# Revit family: IS_21Ventuno_T0155_BIM_IT
name_source: partatom
category: Plumbing Fixtures
revit_build: Autodesk Revit 2017 (Build: 20160225_1515(x64)
units: mm (PartAtom-declared; Revit-internal decimal feet)

## family parameters
Always vertical = No
Cut with Voids When Loaded = No
OmniClass Number = 23.45.05.14.14
OmniClass Title = Sinks/Lavatories
Part Type = Normal
Room Calculation Point = No
Round Connector Dimension = Use Diameter
Shared = No
Work Plane-Based = No

## types (1)
- T015501 - 21/VENTUNO LAVABO 75X52 BEU
    Accessori = www.idealstandard.it
    AltezzaNominale = 198 mm
    Autore = Ideal Standard
    BIMobject category = Basins
    BIMobject category code = sanitary-basins
    BIMobject main category = Sanitary
    BIMobject main category code = sanitary
    BOSUseNativeGeometries = 1
    Brand = Ideal Standard
    Brand url = http://www.idealstandard.it
    Caratteristiche = 21-Lavabo 750 mm
    CodiceABarre = 8014140342472
    CodiceDiPrestazione = EN
    Colore = Bianco
    Connessione = piombatura
    CostoDiSostituzione = 0 $
    Date of publishing = 2019_01_04
    Description = 21-Lavabo 750 mm
    DescrizioneClassifcazioneUni2015 = Wall-hung wash basins
    Desrizione = 21-Lavabo 750 mm
    Dimensione = 1850 x 820 x 820 mm
    DimensioneScarico = 0
    EAN code = https://8014140342472
    Edition number = 1
    Finitura = Bianca
    Forma = scolpito
    Garanzia = Garanzia Ideal Standard
    Grado = n/s
    IFC Classification = IfcSanitaryTerminal
    IfcEsportaCome = SanitaryTerminal
    InformazioniDiProdotto = http://www.idealstandard.it
    Installation instructions = http://www.idealstandard.it
    Installazione = http://www.idealstandard.it
    InstruzioniInstallazione = http://www.idealstandard.it
    LarghezzaNominale = 751 mm
    LunghezzaNominale = 515 mm
    Maniglia = No
    Manufacturer name = Ideal Standard
    Material main = Ceramics
    Materiale = Ceramics
    Model = T015501
    ModelloDiRiferimento = 21-Lavabo 750 mm
    NBS Reference Code = 45-35-70/369
    NBS Reference Description = Wall-Hung Wash Basins
    Nome = WashBasinSystems_21Ventuno_T015501_IdealStandard
    NomeOggettoBim = ISI_IdealStandard_WashBasinSystems_21Ventuno_T015501
    Nominal depth = 0
    Nominal height = 0
    NominalHeight = 198 mm
    NominalLength = 515 mm
    NominalWidth = 751 mm
    NumeroDiModello = T015401
    OmniClass Code = 23-31 13 00
    OmniClass Description = Sinks
    PartiDiRicambio = http://www.idealstandard.it
    PesoNetto = 20.5
    PiattoDoccia = No
    Product Guid = ec9c83e5-59f1-4d8d-9583-9215dccaf0eb
    Product SKU = T0155
    Product certification = http://www.idealstandard.it
    Product data url = https://bimobject.com
    Product family = Sanitary
    Product group = WC pans
    Product name = 21/VENTUNO WASHBASIN 75X52 WHITE
    Product url = http://www.idealstandard.it
    ProfonditaNominale = 0 mm  [stored 0 ft]
    QR code = http://bimobject.com
    Revisione = 1
    RiferimentoClassificazioneUni2015 = Pr_40_20_93_89
    SeatMaterial = 0 mm  [stored 0 ft]
    Size = 1850 x 820 x 820 mm
    SpessoreDelMateriale = 0
    SpilloverLivello = 0
    Technical description = http://www.idealstandard.it
    Telefono = 800 652 290
    TipoDiDato = Fisso
    TipoEspotazioneIfc = IfcSanitaryTerminalType
    URL = http://www.idealstandard.it
    Uniclass 2.0 Code = PR-35-93-95
    Uniclass 2.0 Description = Wc Seats And Covers
    Uniclass 2015 Code = Pr_40_20_93_89
    Uniclass 2015 Name = Wall-hung wash basins
    UnitàDurata = anni
    UnitàDurataGaranzia = anni
    UnitàLineare = millimetri
    UnitàMonetaria = €
    UnitàSuperficie = €
    UnitàVolume = millimetri
    Versione = 1
    VersioneClassificazioneUni2015 = 1
    Weight Net (Kg) = 0
    Youtube clip = https://www.youtube.com

note: [stored X ft] marks values corroborated as IEEE doubles in the binary element streams (Revit-internal decimal feet)

## geometry (parser evidence)
native form markers: Sweep x2
no freeform markers — native parametric forms only
